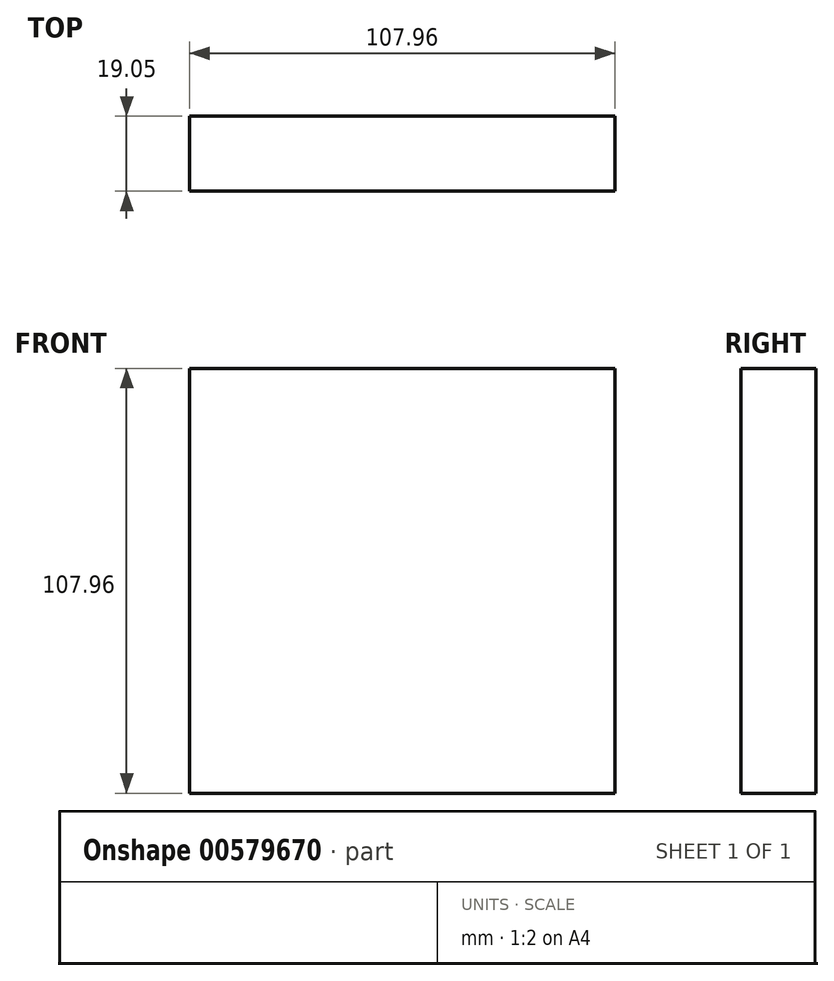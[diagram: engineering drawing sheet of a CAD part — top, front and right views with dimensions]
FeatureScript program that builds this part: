
annotation { "Feature Type Name" : "Feature", "Feature Type Description" : "" }
export const myFeature = defineFeature(function(context is Context, id is Id, definition is map)
    precondition{}
    {
        {
            var Q0;
            Q0=qCreatedBy(makeId("Front.planeOp"),FACE);
            var sketch = newSketch(context, id + "F0", { "sketchPlane" : qUnion([Q0])});
            skLineSegment(sketch, "E0.bottom", {"start": v(53.97, 53.97) * mm, "end": v(-53.97, 53.97) * mm});
            skLineSegment(sketch, "E0.top", {"start": v(53.97, -53.97) * mm, "end": v(-53.97, -53.97) * mm});
            skLineSegment(sketch, "E0.left", {"start": v(53.97, 53.97) * mm, "end": v(53.97, -53.97) * mm});
            skLineSegment(sketch, "E0.right", {"start": v(-53.97, 53.97) * mm, "end": v(-53.97, -53.97) * mm});
            skPoint(sketch, "E0.middle", {"position": v(0, 0) * mm});
            skSolve(sketch);
        }
        {
            var Q0;
            Q0=makeQuery(id+"F0.imprint","IMPRINT",FACE,{"disambiguationData":[TD([[makeQuery(id+"F0.imprint","IMPRINT",EDGE,{"derivedFrom":sQuery(id+"F0.wireOp",EDGE,"E0.bottom")}),1.0]])]});
            extrude(context, id + "F1", {"entities" : qUnion([Q0]), "depth" : 19.05 * mm, "offsetDistance" : 25.4 * mm});
        }
    });
